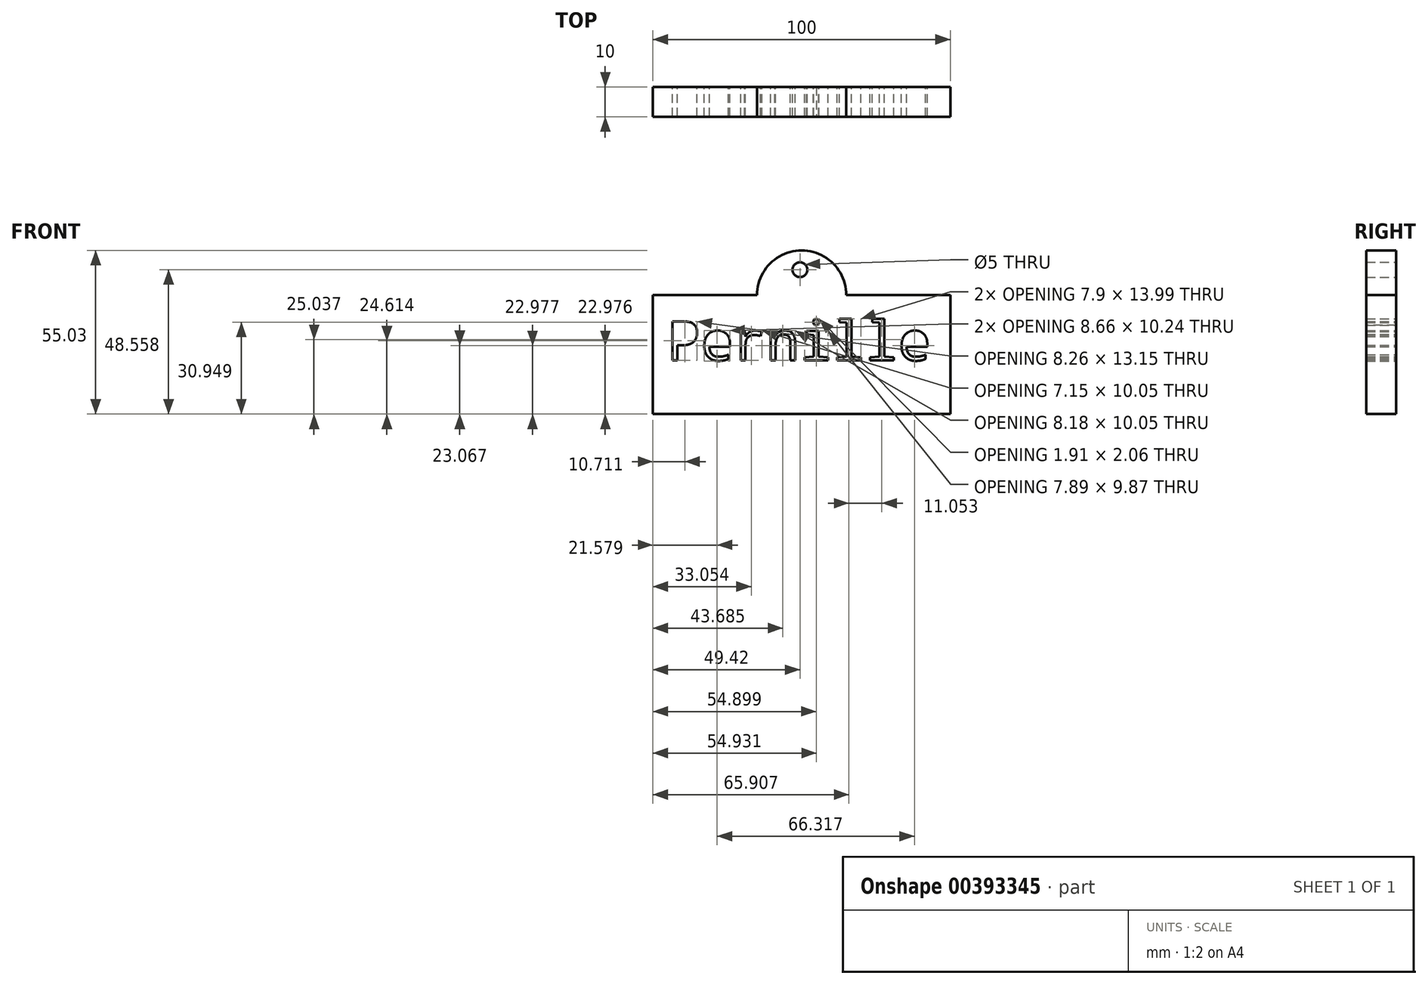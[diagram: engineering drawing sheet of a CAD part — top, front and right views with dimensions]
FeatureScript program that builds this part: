
annotation { "Feature Type Name" : "Feature", "Feature Type Description" : "" }
export const myFeature = defineFeature(function(context is Context, id is Id, definition is map)
    precondition{}
    {
        {
            var Q0;
            Q0=qCreatedBy(makeId("Front.planeOp"),FACE);
            var sketch = newSketch(context, id + "F0", { "sketchPlane" : qUnion([Q0])});
            skLineSegment(sketch, "E0.top", {"start": v(-49.42, 12.8) * mm, "end": v(50.58, 12.8) * mm});
            skLineSegment(sketch, "E0.left", {"start": v(-49.42, 52.8) * mm, "end": v(-49.42, 12.8) * mm});
            skLineSegment(sketch, "E0.right", {"start": v(50.58, 52.8) * mm, "end": v(50.58, 12.8) * mm});
            skPoint(sketch, "E1", {"position": v(0.58, 52.8) * mm});
            skPoint(sketch, "E2", {"position": v(-14.42, 52.8) * mm});
            skPoint(sketch, "E3", {"position": v(15.58, 52.8) * mm});
            skArc(sketch, "E4", {"start": v(15.58, 52.8) * mm, "mid": v(0.58, 67.83) * mm, "end": v(-14.42, 52.8) * mm});
            skLineSegment(sketch, "E5", {"start": v(-49.42, 52.8) * mm, "end": v(-14.42, 52.8) * mm});
            skLineSegment(sketch, "E6", {"start": v(15.58, 52.8) * mm, "end": v(50.58, 52.8) * mm});
            skCircle(sketch, "E7", {"center": v(0, 61.36) * mm, "radius": 2.5 * mm});
            skText(sketch, "E8", { "text": "Pernille ", "fontName": "DroidSansMono.ttf"});
            const initialGuessF0  = {"E8": [-0.04442, 0.03084, 1, 0, 0.01326]};
            skSetInitialGuess(sketch, initialGuessF0);
            skSolve(sketch);
        }
        {
            var Q0;
            Q0=makeQuery(id+"F0.imprint","IMPRINT",FACE,{"disambiguationData":[TD([[makeQuery(id+"F0.imprint","IMPRINT",EDGE,{"derivedFrom":sQuery(id+"F0.wireOp",EDGE,"E0.top")}),1.0]])]});
            extrude(context, id + "F1", {"entities" : qUnion([Q0]), "depth" : 10 * mm});
        }
    });
